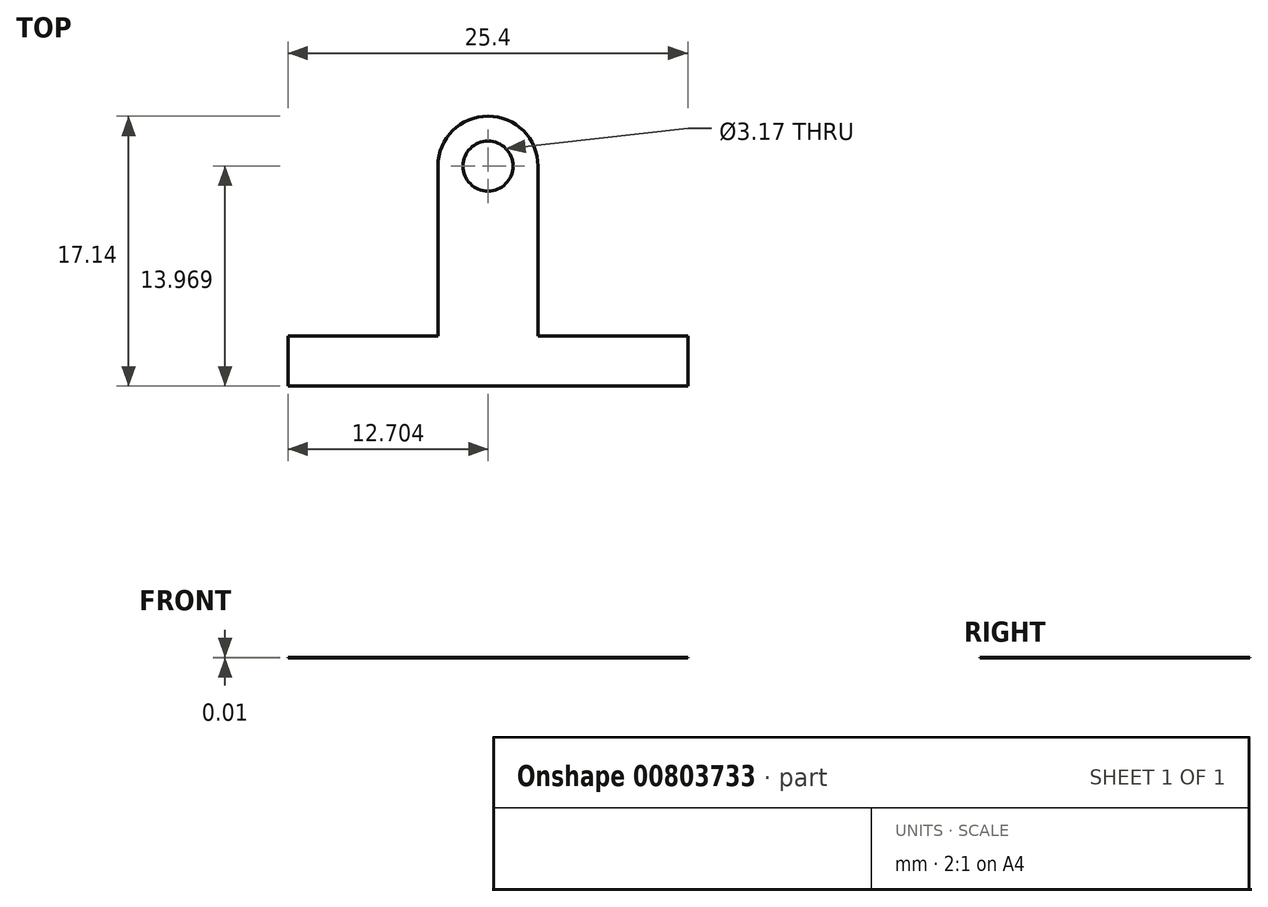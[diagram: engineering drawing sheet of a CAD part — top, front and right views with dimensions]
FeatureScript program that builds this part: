
annotation { "Feature Type Name" : "Feature", "Feature Type Description" : "" }
export const myFeature = defineFeature(function(context is Context, id is Id, definition is map)
    precondition{}
    {
        {
            var Q0;
            Q0=qCreatedBy(makeId("Top.planeOp"),FACE);
            var sketch = newSketch(context, id + "F0", { "sketchPlane" : qUnion([Q0])});
            skLineSegment(sketch, "E0.top", {"start": v(-7.85, -4.38) * mm, "end": v(17.55, -4.38) * mm});
            skLineSegment(sketch, "E0.left", {"start": v(-7.85, -1.2) * mm, "end": v(-7.85, -4.38) * mm});
            skLineSegment(sketch, "E0.right", {"start": v(17.55, -1.2) * mm, "end": v(17.55, -4.38) * mm});
            skLineSegment(sketch, "E1.bottom", {"start": v(1.68, -1.2) * mm, "end": v(8.03, -1.2) * mm});
            skLineSegment(sketch, "E1.top", {"start": v(4.85, 12.76) * mm, "end": v(4.85, 12.76) * mm});
            skLineSegment(sketch, "E1.left", {"start": v(1.68, -1.2) * mm, "end": v(1.68, 9.59) * mm});
            skLineSegment(sketch, "E1.right", {"start": v(8.03, -1.2) * mm, "end": v(8.03, 9.59) * mm});
            skCircle(sketch, "E2", {"center": v(4.85, 9.59) * mm, "radius": 1.59 * mm});
            skPoint(sketch, "E2.centerSnap0", {"position": v(4.85, -1.2) * mm});
            skLineSegment(sketch, "E3", {"start": v(1.68, -1.2) * mm, "end": v(-7.85, -1.2) * mm});
            skLineSegment(sketch, "E4", {"start": v(8.03, -1.2) * mm, "end": v(17.55, -1.2) * mm});
            skPoint(sketch, "E5.visualSharp", {"position": v(1.68, 12.76) * mm});
            skArc(sketch, "E5.filletArc", {"start": v(4.85, 12.76) * mm, "mid": v(2.6, 11.83) * mm, "end": v(1.68, 9.59) * mm});
            skPoint(sketch, "E6.visualSharp", {"position": v(8.03, 12.76) * mm});
            skArc(sketch, "E6.filletArc", {"start": v(8.03, 9.59) * mm, "mid": v(7.1, 11.83) * mm, "end": v(4.85, 12.76) * mm});
            skLineSegment(sketch, "E7", {"start": v(8.03, 9.59) * mm, "end": v(4.85, 9.59) * mm});
            skSolve(sketch);
        }
        {
            var Q0;
            Q0=makeQuery(id+"F0.imprint","IMPRINT",FACE,{"disambiguationData":[TD([[makeQuery(id+"F0.imprint","IMPRINT",EDGE,{"derivedFrom":sQuery(id+"F0.wireOp",EDGE,"E1.bottom")}),1.0]])]});
            var Q1;
            Q1=makeQuery(id+"F0.imprint","IMPRINT",FACE,{"disambiguationData":[TD([[makeQuery(id+"F0.imprint","IMPRINT",EDGE,{"derivedFrom":sQuery(id+"F0.wireOp",EDGE,"E0.top")}),1.0]])]});
            extrude(context, id + "F1", {"entities" : qUnion([Q0, Q1]), "depth" : .75 / 50.8 * mm, "offsetDistance" : 25.4 * mm});
        }
        {
            var Q0;
            Q0=makeQuery(id+"F1.opExtrude","SWEPT_FACE",FACE,{"disambiguationData":[OSD([sQuery(id+"F0.wireOp",EDGE,"E4")])]});
            var sketch = newSketch(context, id + "F2", { "sketchPlane" : qUnion([Q0])});
            skLineSegment(sketch, "E8", {"start": v(-17.55, 4.76) * mm, "end": v(-8.03, 4.76) * mm});
            skPoint(sketch, "E9", {"position": v(-12.8, 4.76) * mm});
            skSolve(sketch);
        }
        {
            var Q0;
            Q0=sQuery(id+"F2.wireOp",VERTEX,"E9");
            var Q1;
            Q1=makeQuery(id+"F1.opExtrude","SWEPT_BODY",BODY,{"disambiguationData":[OSD([sQuery(id+"F0.wireOp",EDGE,"E0.top"),sQuery(id+"F0.wireOp",EDGE,"E0.left"),sQuery(id+"F0.wireOp",EDGE,"E0.right"),sQuery(id+"F0.wireOp",EDGE,"E1.left"),sQuery(id+"F0.wireOp",EDGE,"E1.right"),sQuery(id+"F0.wireOp",EDGE,"E2"),sQuery(id+"F0.wireOp",EDGE,"E3"),sQuery(id+"F0.wireOp",EDGE,"E4"),sQuery(id+"F0.wireOp",EDGE,"E5.filletArc"),sQuery(id+"F0.wireOp",EDGE,"E6.filletArc")])]});
            hole(context, id + "F3", {"style" : HoleStyle.SIMPLE, "endStyle" : HoleEndStyle.THROUGH, "holeDiameter" : 3.17 * mm, "majorDiameter" : 6.35 * mm, "isTappedThrough" : true, "tappedDepth" : 12.7 * mm, "tapClearance" : 3, "locations" : qUnion([Q0]), "scope" : qUnion([Q1])});
        }
        {
            var Q0;
            Q0=makeQuery(id+"F1.opExtrude","SWEPT_FACE",FACE,{"disambiguationData":[OSD([sQuery(id+"F0.wireOp",EDGE,"E3")])]});
            var sketch = newSketch(context, id + "F4", { "sketchPlane" : qUnion([Q0])});
            skLineSegment(sketch, "E10", {"start": v(-1.68, 4.76) * mm, "end": v(7.85, 4.76) * mm});
            skPoint(sketch, "E11", {"position": v(3.08, 4.76) * mm});
            skSolve(sketch);
        }
        {
            var Q0;
            Q0=sQuery(id+"F4.wireOp",VERTEX,"E11");
            var Q1;
            Q1=makeQuery(id+"F1.opExtrude","SWEPT_BODY",BODY,{"disambiguationData":[OSD([sQuery(id+"F0.wireOp",EDGE,"E0.top"),sQuery(id+"F0.wireOp",EDGE,"E0.left"),sQuery(id+"F0.wireOp",EDGE,"E0.right"),sQuery(id+"F0.wireOp",EDGE,"E1.left"),sQuery(id+"F0.wireOp",EDGE,"E1.right"),sQuery(id+"F0.wireOp",EDGE,"E2"),sQuery(id+"F0.wireOp",EDGE,"E3"),sQuery(id+"F0.wireOp",EDGE,"E4"),sQuery(id+"F0.wireOp",EDGE,"E5.filletArc"),sQuery(id+"F0.wireOp",EDGE,"E6.filletArc")])]});
            hole(context, id + "F5", {"style" : HoleStyle.SIMPLE, "endStyle" : HoleEndStyle.THROUGH, "holeDiameter" : 3.17 * mm, "majorDiameter" : 6.35 * mm, "isTappedThrough" : true, "tappedDepth" : 12.7 * mm, "tapClearance" : 3, "locations" : qUnion([Q0]), "scope" : qUnion([Q1])});
        }
    });
